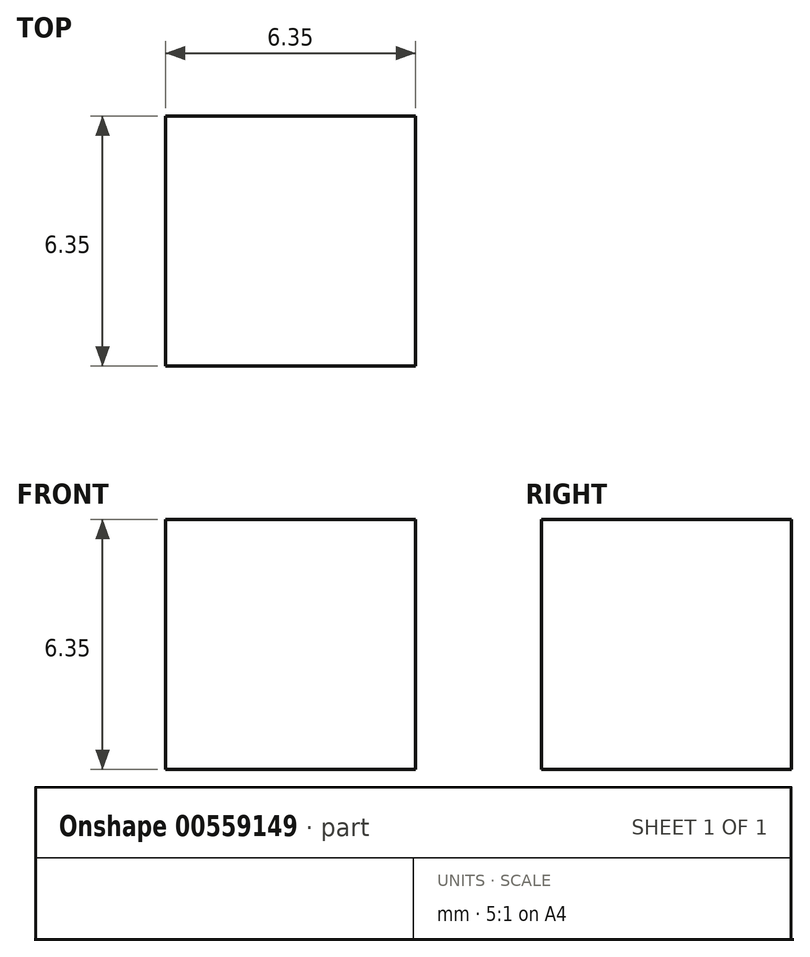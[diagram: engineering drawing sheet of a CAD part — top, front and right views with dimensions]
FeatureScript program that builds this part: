
annotation { "Feature Type Name" : "Feature", "Feature Type Description" : "" }
export const myFeature = defineFeature(function(context is Context, id is Id, definition is map)
    precondition{}
    {
        {
            var Q0;
            Q0=qCreatedBy(makeId("Top.planeOp"),FACE);
            var sketch = newSketch(context, id + "F0", { "sketchPlane" : qUnion([Q0])});
            skLineSegment(sketch, "E0.bottom", {"start": v(0, 0) * mm, "end": v(6.35, 0) * mm});
            skLineSegment(sketch, "E0.top", {"start": v(0, 6.35) * mm, "end": v(6.35, 6.35) * mm});
            skLineSegment(sketch, "E0.left", {"start": v(0, 0) * mm, "end": v(0, 6.35) * mm});
            skLineSegment(sketch, "E0.right", {"start": v(6.35, 0) * mm, "end": v(6.35, 6.35) * mm});
            skSolve(sketch);
        }
        {
            var Q0;
            Q0 = qSketchRegion(id + "F0", true);
            extrude(context, id + "F1", {"entities" : qUnion([Q0]), "depth" : 6.35 * mm, "offsetDistance" : 25.4 * mm});
        }
    });
